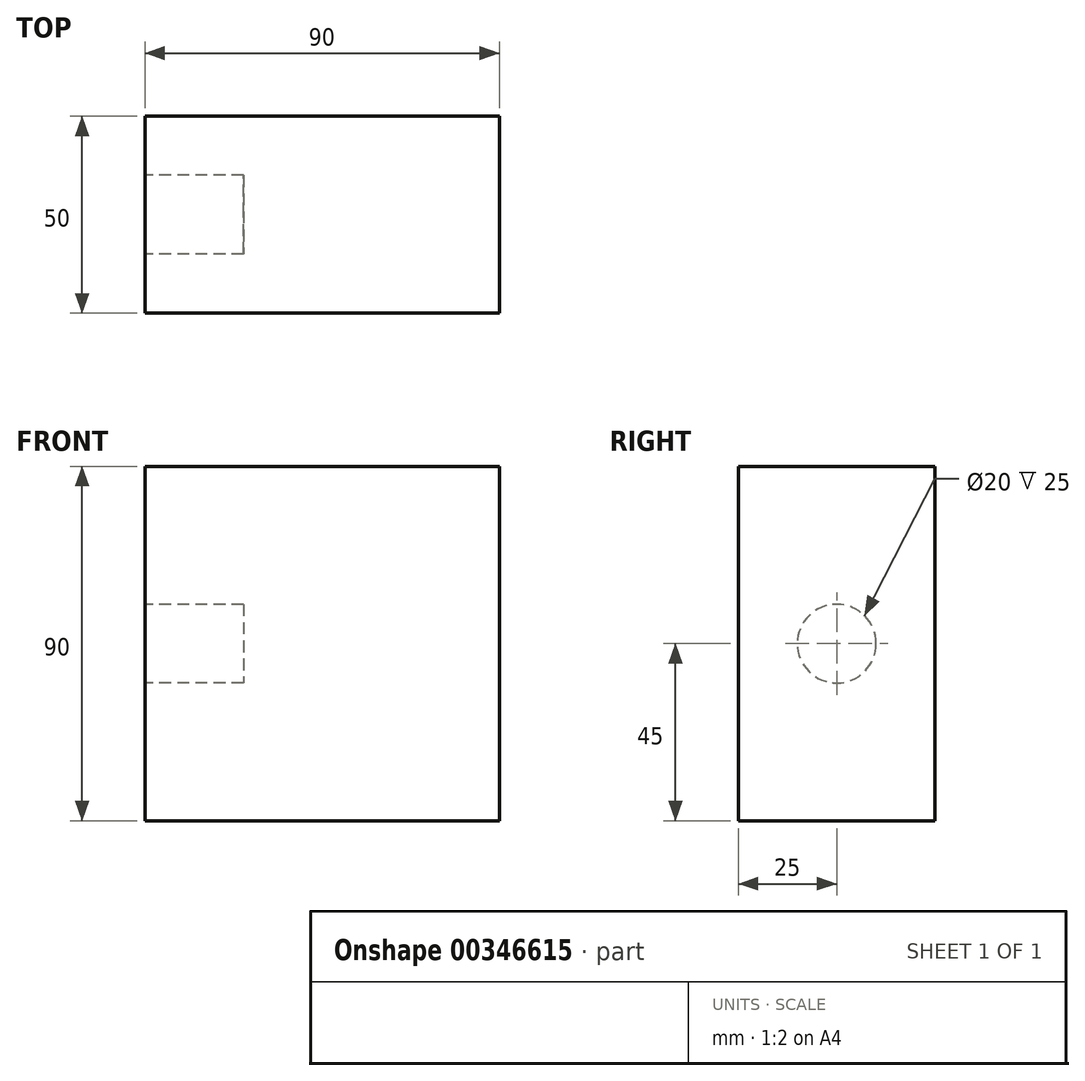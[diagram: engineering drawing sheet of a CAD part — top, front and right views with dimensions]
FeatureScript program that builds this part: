
annotation { "Feature Type Name" : "Feature", "Feature Type Description" : "" }
export const myFeature = defineFeature(function(context is Context, id is Id, definition is map)
    precondition{}
    {
        {
            var Q0;
            Q0=qCreatedBy(makeId("Front.planeOp"),FACE);
            var sketch = newSketch(context, id + "F0", { "sketchPlane" : qUnion([Q0])});
            skLineSegment(sketch, "E0.bottom", {"start": v(0, 0) * mm, "end": v(90, 0) * mm});
            skLineSegment(sketch, "E0.top", {"start": v(0, -90) * mm, "end": v(90, -90) * mm});
            skLineSegment(sketch, "E0.left", {"start": v(0, 0) * mm, "end": v(0, -90) * mm});
            skLineSegment(sketch, "E0.right", {"start": v(90, 0) * mm, "end": v(90, -90) * mm});
            skSolve(sketch);
        }
        {
            var Q0;
            Q0 = qSketchRegion(id + "F0", true);
            extrude(context, id + "F1", {"entities" : qUnion([Q0]), "depth" : 50 * mm});
        }
        {
            var Q0;
            Q0=makeQuery(id+"F1.opExtrude","SWEPT_FACE",FACE,{"disambiguationData":[OSD([sQuery(id+"F0.wireOp",EDGE,"E0.left")])]});
            var sketch = newSketch(context, id + "F2", { "sketchPlane" : qUnion([Q0])});
            skLineSegment(sketch, "E1", {"start": v(50, -45) * mm, "end": v(0, -45) * mm, "construction": true});
            skCircle(sketch, "E2", {"center": v(25, -45) * mm, "radius": 10 * mm});
            skSolve(sketch);
        }
        {
            var Q0;
            Q0 = qSketchRegion(id + "F2", true);
            extrude(context, id + "F3", {"entities" : qUnion([Q0]), "operationType" : NewBodyOperationType.REMOVE, "oppositeDirection" : true, "depth" : 25 * mm});
        }
    });
